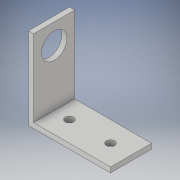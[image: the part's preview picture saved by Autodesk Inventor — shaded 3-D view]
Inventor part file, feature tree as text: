
AUTODESK INVENTOR PART (.ipt)
format: ipt  version: 2018 (Build 220112000, 112)  size: 122,880 bytes
history: native  units: in
note: dims shown in document units (in); Inventor stores cm internally (conversion verified against a paired STEP export)
features: extrude x3, sketch x3
ambient origin geometry x8: Origin, YZ Plane, XZ Plane, XY Plane, X Axis, Y Axis, Z Axis, Center Point
bodies: Solid1 (feature_tree)
feature tree (6):
  extrude  "Extrusion1"  Depth=2.0in
  extrude  "Extrusion2"  Depth=0.125in
  extrude  "Extrusion4"  Depth=1.0in
  sketch  "Sketch1"  dims[d0=0.125in d1=2.0in]
  sketch  "Sketch2"  dims[d2=2.0in d3=0.125in]
  sketch  "Sketch3"  dims[d4=1.0in d5=0.0in d6=1.0in d7=0.6225in d8=1.0in d9=0.0in d10=0.5in d11=180.0deg d12=0.2031in d15=1.0in d16=1.0in d17=0.0in]
